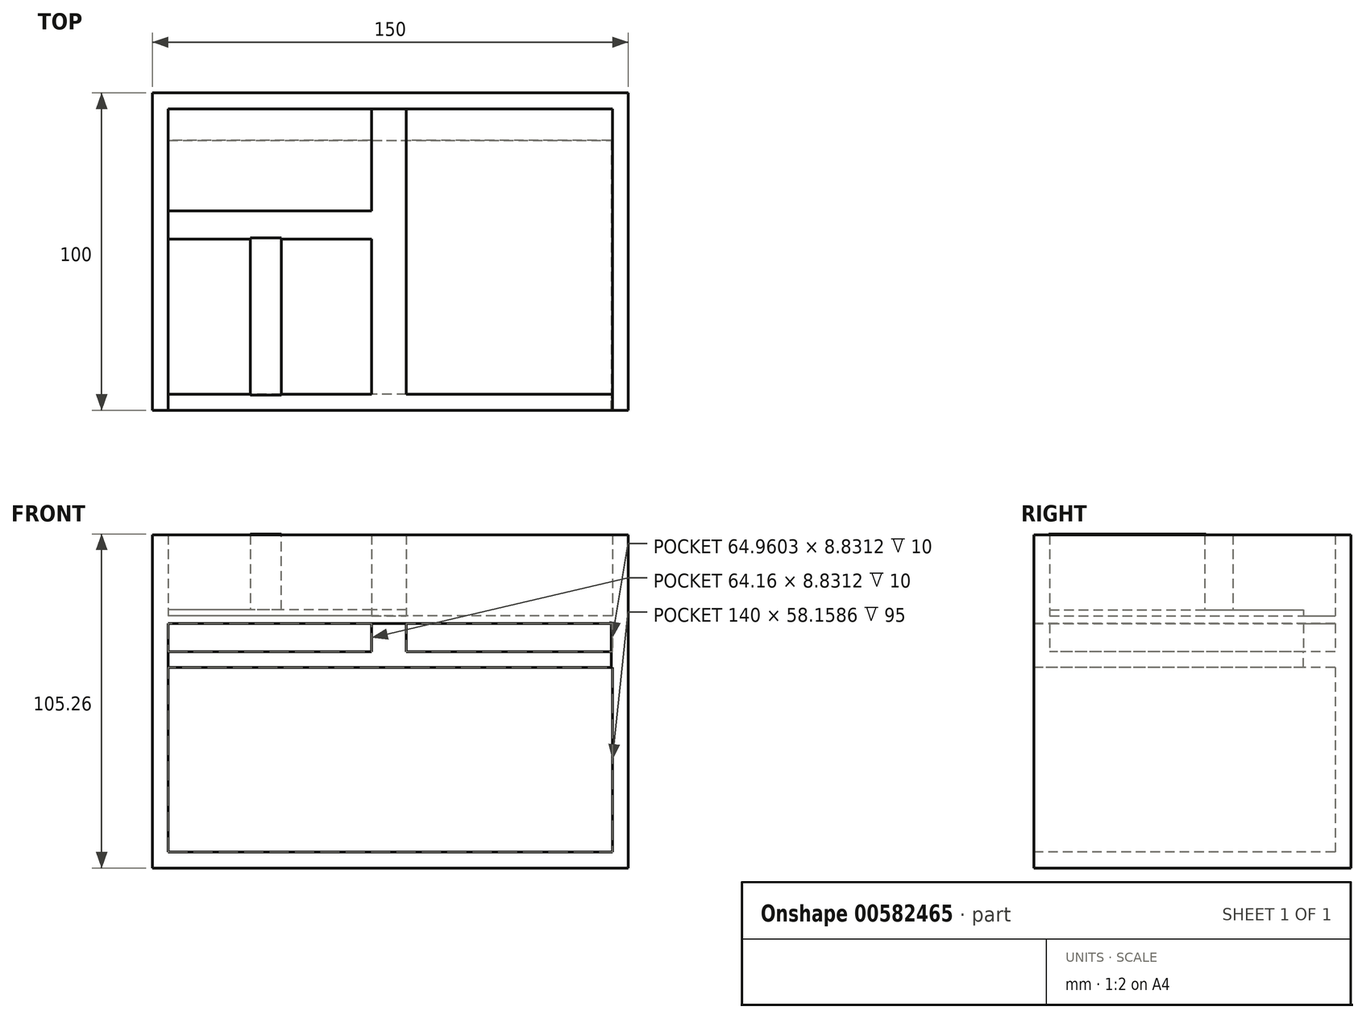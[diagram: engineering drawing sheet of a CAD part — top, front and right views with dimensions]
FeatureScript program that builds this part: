
annotation { "Feature Type Name" : "Feature", "Feature Type Description" : "" }
export const myFeature = defineFeature(function(context is Context, id is Id, definition is map)
    precondition{}
    {
        {
            var Q0;
            Q0=qCreatedBy(makeId("Top.planeOp"),FACE);
            var sketch = newSketch(context, id + "F0", { "sketchPlane" : qUnion([Q0])});
            skLineSegment(sketch, "E0.bottom", {"start": v(-111.6, 82.15) * mm, "end": v(38.4, 82.15) * mm});
            skLineSegment(sketch, "E0.top", {"start": v(-111.6, -17.85) * mm, "end": v(38.4, -17.85) * mm});
            skLineSegment(sketch, "E0.left", {"start": v(-111.6, 82.15) * mm, "end": v(-111.6, -17.85) * mm});
            skLineSegment(sketch, "E0.right", {"start": v(38.4, 82.15) * mm, "end": v(38.4, -17.85) * mm});
            skSolve(sketch);
        }
        {
            var Q0;
            Q0=makeQuery(id+"F0.imprint","IMPRINT",FACE,{"disambiguationData":[TD([[makeQuery(id+"F0.imprint","IMPRINT",EDGE,{"derivedFrom":sQuery(id+"F0.wireOp",EDGE,"E0.bottom")}),-1.0]])]});
            extrude(context, id + "F1", {"entities" : qUnion([Q0]), "depth" : 5 * mm, "offsetDistance" : 25 * mm});
        }
        {
            var Q0;
            Q0=makeQuery(id+"F1.opExtrude","CAP_FACE",FACE,{"disambiguationData":[OSD([sQuery(id+"F0.wireOp",EDGE,"E0.bottom"),sQuery(id+"F0.wireOp",EDGE,"E0.top"),sQuery(id+"F0.wireOp",EDGE,"E0.left"),sQuery(id+"F0.wireOp",EDGE,"E0.right")])],"isStart":false});
            var sketch = newSketch(context, id + "F2", { "sketchPlane" : qUnion([Q0])});
            skLineSegment(sketch, "E1.bottom", {"start": v(-111.6, 82.15) * mm, "end": v(-106.6, 82.15) * mm});
            skLineSegment(sketch, "E1.top", {"start": v(-111.6, -17.85) * mm, "end": v(-106.6, -17.85) * mm});
            skLineSegment(sketch, "E1.left", {"start": v(-111.6, 82.15) * mm, "end": v(-111.6, -17.85) * mm});
            skLineSegment(sketch, "E1.right", {"start": v(-106.6, 82.15) * mm, "end": v(-106.6, -17.85) * mm});
            skSolve(sketch);
        }
        {
            var Q0;
            Q0=makeQuery(id+"F2.imprint","IMPRINT",FACE,{"disambiguationData":[TD([[makeQuery(id+"F2.imprint","IMPRINT",EDGE,{"derivedFrom":sQuery(id+"F2.wireOp",EDGE,"E1.bottom")}),-1.0]])]});
            extrude(context, id + "F3", {"entities" : qUnion([Q0]), "operationType" : NewBodyOperationType.ADD, "depth" : 100 * mm, "offsetDistance" : 25 * mm});
        }
        {
            var Q0;
            Q0=makeQuery(id+"F1.opExtrude","CAP_FACE",FACE,{"disambiguationData":[OSD([sQuery(id+"F0.wireOp",EDGE,"E0.bottom"),sQuery(id+"F0.wireOp",EDGE,"E0.top"),sQuery(id+"F0.wireOp",EDGE,"E0.left"),sQuery(id+"F0.wireOp",EDGE,"E0.right")])],"isStart":false});
            var sketch = newSketch(context, id + "F4", { "sketchPlane" : qUnion([Q0])});
            skLineSegment(sketch, "E2.bottom", {"start": v(-106.6, 82.15) * mm, "end": v(38.4, 82.15) * mm});
            skLineSegment(sketch, "E2.top", {"start": v(-106.6, 77.15) * mm, "end": v(38.4, 77.15) * mm});
            skLineSegment(sketch, "E2.left", {"start": v(-106.6, 82.15) * mm, "end": v(-106.6, 77.15) * mm});
            skLineSegment(sketch, "E2.right", {"start": v(38.4, 82.15) * mm, "end": v(38.4, 77.15) * mm});
            skSolve(sketch);
        }
        {
            var Q0;
            Q0=makeQuery(id+"F4.imprint","IMPRINT",FACE,{"disambiguationData":[TD([[makeQuery(id+"F4.imprint","IMPRINT",EDGE,{"derivedFrom":sQuery(id+"F4.wireOp",EDGE,"E2.bottom")}),-1.0]])]});
            extrude(context, id + "F5", {"entities" : qUnion([Q0]), "operationType" : NewBodyOperationType.ADD, "depth" : 100 * mm, "offsetDistance" : 25 * mm});
        }
        {
            var Q0;
            Q0=makeQuery(id+"F1.opExtrude","CAP_FACE",FACE,{"disambiguationData":[OSD([sQuery(id+"F0.wireOp",EDGE,"E0.bottom"),sQuery(id+"F0.wireOp",EDGE,"E0.top"),sQuery(id+"F0.wireOp",EDGE,"E0.left"),sQuery(id+"F0.wireOp",EDGE,"E0.right")])],"isStart":false});
            var sketch = newSketch(context, id + "F6", { "sketchPlane" : qUnion([Q0])});
            skLineSegment(sketch, "E3.bottom", {"start": v(38.4, 77.15) * mm, "end": v(33.4, 77.15) * mm});
            skLineSegment(sketch, "E3.top", {"start": v(38.4, -17.85) * mm, "end": v(33.4, -17.85) * mm});
            skLineSegment(sketch, "E3.left", {"start": v(38.4, 77.15) * mm, "end": v(38.4, -17.85) * mm});
            skLineSegment(sketch, "E3.right", {"start": v(33.4, 77.15) * mm, "end": v(33.4, -17.85) * mm});
            skSolve(sketch);
        }
        {
            var Q0;
            Q0=makeQuery(id+"F6.imprint","IMPRINT",FACE,{"disambiguationData":[TD([[makeQuery(id+"F6.imprint","IMPRINT",EDGE,{"derivedFrom":sQuery(id+"F6.wireOp",EDGE,"E3.bottom")}),-1.0]])]});
            extrude(context, id + "F7", {"entities" : qUnion([Q0]), "operationType" : NewBodyOperationType.ADD, "depth" : 100 * mm, "offsetDistance" : 25 * mm});
        }
        {
            var Q0;
            Q0=makeQuery(id+"F7.boolean.opBoolean","MERGE",FACE,{"derivedFrom":[makeQuery(id+"F3.boolean.opBoolean","MERGE",FACE,{"derivedFrom":[makeQuery(id+"F1.opExtrude","SWEPT_FACE",FACE,{"disambiguationData":[OSD([sQuery(id+"F0.wireOp",EDGE,"E0.top")])]}),makeQuery(id+"F3.opExtrude","SWEPT_FACE",FACE,{"disambiguationData":[OSD([sQuery(id+"F2.wireOp",EDGE,"E1.top")])]})]}),makeQuery(id+"F7.opExtrude","SWEPT_FACE",FACE,{"disambiguationData":[OSD([sQuery(id+"F6.wireOp",EDGE,"E3.top")])]})]});
            var sketch = newSketch(context, id + "F8", { "sketchPlane" : qUnion([Q0])});
            skLineSegment(sketch, "E4.bottom", {"start": v(-106.6, 68.16) * mm, "end": v(33.4, 68.16) * mm});
            skLineSegment(sketch, "E4.top", {"start": v(-106.6, 63.16) * mm, "end": v(33.4, 63.16) * mm});
            skLineSegment(sketch, "E4.left", {"start": v(-106.6, 68.16) * mm, "end": v(-106.6, 63.16) * mm});
            skLineSegment(sketch, "E4.right", {"start": v(33.4, 68.16) * mm, "end": v(33.4, 63.16) * mm});
            skSolve(sketch);
        }
        {
            var Q0;
            Q0=makeQuery(id+"F8.imprint","IMPRINT",FACE,{"disambiguationData":[TD([[makeQuery(id+"F8.imprint","IMPRINT",EDGE,{"derivedFrom":sQuery(id+"F8.wireOp",EDGE,"E4.bottom")}),-1.0]])]});
            extrude(context, id + "F9", {"entities" : qUnion([Q0]), "operationType" : NewBodyOperationType.ADD, "oppositeDirection" : true, "depth" : 100 * mm, "offsetDistance" : 25 * mm});
        }
        {
            var Q0;
            Q0=makeQuery(id+"F9.opExtrude","SWEPT_FACE",FACE,{"disambiguationData":[OSD([sQuery(id+"F8.wireOp",EDGE,"E4.bottom")])]});
            var sketch = newSketch(context, id + "F10", { "sketchPlane" : qUnion([Q0])});
            skLineSegment(sketch, "E5.bottom", {"start": v(-106.6, -17.85) * mm, "end": v(33.4, -17.85) * mm});
            skLineSegment(sketch, "E5.top", {"start": v(-106.6, -12.85) * mm, "end": v(33.4, -12.85) * mm});
            skLineSegment(sketch, "E5.left", {"start": v(-106.6, -17.85) * mm, "end": v(-106.6, -12.85) * mm});
            skLineSegment(sketch, "E5.right", {"start": v(33.4, -17.85) * mm, "end": v(33.4, -12.85) * mm});
            skSolve(sketch);
        }
        {
            var Q0;
            Q0=makeQuery(id+"F10.imprint","IMPRINT",FACE,{"disambiguationData":[TD([[makeQuery(id+"F10.imprint","IMPRINT",EDGE,{"derivedFrom":sQuery(id+"F10.wireOp",EDGE,"E5.bottom")}),1.0]])]});
            extrude(context, id + "F11", {"entities" : qUnion([Q0]), "operationType" : NewBodyOperationType.ADD, "depth" : 36.8 * mm, "offsetDistance" : 25 * mm});
        }
        {
            var Q0;
            Q0=makeQuery(id+"F9.opExtrude","SWEPT_FACE",FACE,{"disambiguationData":[OSD([sQuery(id+"F8.wireOp",EDGE,"E4.bottom")])]});
            var sketch = newSketch(context, id + "F12", { "sketchPlane" : qUnion([Q0])});
            skLineSegment(sketch, "E6.bottom", {"start": v(-42.44, 77.15) * mm, "end": v(-31.56, 77.15) * mm});
            skLineSegment(sketch, "E6.top", {"start": v(-42.44, -12.85) * mm, "end": v(-31.56, -12.85) * mm});
            skLineSegment(sketch, "E6.left", {"start": v(-42.44, 77.15) * mm, "end": v(-42.44, -12.85) * mm});
            skLineSegment(sketch, "E6.right", {"start": v(-31.56, 77.15) * mm, "end": v(-31.56, -12.85) * mm});
            skSolve(sketch);
        }
        {
            var Q0;
            Q0=makeQuery(id+"F12.imprint","IMPRINT",FACE,{"disambiguationData":[TD([[makeQuery(id+"F12.imprint","IMPRINT",EDGE,{"derivedFrom":sQuery(id+"F12.wireOp",EDGE,"E6.bottom")}),1.0]])]});
            extrude(context, id + "F13", {"entities" : qUnion([Q0]), "operationType" : NewBodyOperationType.ADD, "depth" : 36.8 * mm, "offsetDistance" : 25 * mm});
        }
        {
            var Q0;
            Q0=makeQuery(id+"F13.boolean.opBoolean","SPLIT",FACE,{"disambiguationData":[TD([makeQuery(id+"F3.opExtrude","SWEPT_FACE",FACE,{"disambiguationData":[OSD([sQuery(id+"F2.wireOp",EDGE,"E1.right")])]})])],"derivedFrom":makeQuery(id+"F9.opExtrude","SWEPT_FACE",FACE,{"disambiguationData":[OSD([sQuery(id+"F8.wireOp",EDGE,"E4.bottom")])]})});
            var sketch = newSketch(context, id + "F14", { "sketchPlane" : qUnion([Q0])});
            skSolve(sketch);
        }
        {
            var Q0;
            {var subQ2=sQuery(id+"F12.wireOp",EDGE,"E6.left");Q0=makeQuery(id+"F14.imprint","IMPRINT",FACE,{"disambiguationData":[TD([[makeQuery(id+"F14.imprint","IMPRINT",EDGE,{"derivedFrom":makeQuery(id+"F13.opExtrude","CAP_EDGE",EDGE,{"disambiguationData":[OSD([subQ2])],"isStart":true})}),-1.0]])]});}
            var sketch = newSketch(context, id + "F15", { "sketchPlane" : qUnion([Q0])});
            skLineSegment(sketch, "E7.bottom", {"start": v(-106.58, 44.94) * mm, "end": v(33.5, 44.94) * mm});
            skLineSegment(sketch, "E7.top", {"start": v(-106.58, 36.1) * mm, "end": v(33.5, 36.1) * mm});
            skLineSegment(sketch, "E7.left", {"start": v(-106.58, 44.94) * mm, "end": v(-106.58, 36.1) * mm});
            skLineSegment(sketch, "E7.right", {"start": v(33.5, 44.94) * mm, "end": v(33.5, 36.1) * mm});
            skSolve(sketch);
        }
        {
            var Q0;
            {var subQ0=sQuery(id+"F15.wireOp",EDGE,"E7.left");Q0=makeQuery(id+"F15.imprint","IMPRINT",FACE,{"disambiguationData":[TD([[makeQuery(id+"F15.imprint","IMPRINT",EDGE,{"derivedFrom":subQ0}),1.0]])]});}
            extrude(context, id + "F16", {"entities" : qUnion([Q0]), "operationType" : NewBodyOperationType.ADD, "depth" : 36.8 * mm, "offsetDistance" : 25 * mm});
        }
        {
            var Q0;
            {var subQ2=sQuery(id+"F12.wireOp",EDGE,"E6.left");Q0=makeQuery(id+"F14.imprint","IMPRINT",FACE,{"disambiguationData":[TD([[makeQuery(id+"F14.imprint","IMPRINT",EDGE,{"derivedFrom":makeQuery(id+"F13.opExtrude","CAP_EDGE",EDGE,{"disambiguationData":[OSD([subQ2])],"isStart":true})}),-1.0]])]});}
            var sketch = newSketch(context, id + "F17", { "sketchPlane" : qUnion([Q0])});
            skLineSegment(sketch, "E8.bottom", {"start": v(-80.74, 35.42) * mm, "end": v(-71, 35.42) * mm});
            skLineSegment(sketch, "E8.top", {"start": v(-80.74, -13.08) * mm, "end": v(-71, -13.08) * mm});
            skLineSegment(sketch, "E8.left", {"start": v(-80.74, 35.42) * mm, "end": v(-80.74, -13.08) * mm});
            skLineSegment(sketch, "E8.right", {"start": v(-71, 35.42) * mm, "end": v(-71, -13.08) * mm});
            skSolve(sketch);
        }
        {
            var Q0;
            Q0 = qSketchRegion(id + "F17", true);
            extrude(context, id + "F18", {"entities" : qUnion([Q0]), "operationType" : NewBodyOperationType.ADD, "depth" : 37.1 * mm, "offsetDistance" : 25 * mm});
        }
        {
            var Q0;
            Q0=makeQuery(id+"F18.opExtrude","SWEPT_FACE",FACE,{"disambiguationData":[OSD([sQuery(id+"F17.wireOp",EDGE,"E8.bottom")])]});
            extrude(context, id + "F19", {"entities" : qUnion([Q0]), "operationType" : NewBodyOperationType.ADD, "depth" : 1 * mm, "offsetDistance" : 25 * mm});
        }
        {
            var Q0;
            Q0=makeQuery(id+"F11.boolean.opBoolean","MERGE",FACE,{"derivedFrom":[makeQuery(id+"F9.boolean.opBoolean","MERGE",FACE,{"derivedFrom":[makeQuery(id+"F7.boolean.opBoolean","MERGE",FACE,{"derivedFrom":[makeQuery(id+"F3.boolean.opBoolean","MERGE",FACE,{"derivedFrom":[makeQuery(id+"F1.opExtrude","SWEPT_FACE",FACE,{"disambiguationData":[OSD([sQuery(id+"F0.wireOp",EDGE,"E0.top")])]}),makeQuery(id+"F3.opExtrude","SWEPT_FACE",FACE,{"disambiguationData":[OSD([sQuery(id+"F2.wireOp",EDGE,"E1.top")])]})]}),makeQuery(id+"F7.opExtrude","SWEPT_FACE",FACE,{"disambiguationData":[OSD([sQuery(id+"F6.wireOp",EDGE,"E3.top")])]})]}),makeQuery(id+"F9.opExtrude","CAP_FACE",FACE,{"disambiguationData":[OSD([sQuery(id+"F8.wireOp",EDGE,"E4.bottom"),sQuery(id+"F8.wireOp",EDGE,"E4.top"),sQuery(id+"F8.wireOp",EDGE,"E4.left"),sQuery(id+"F8.wireOp",EDGE,"E4.right")])],"isStart":true})]}),makeQuery(id+"F11.opExtrude","SWEPT_FACE",FACE,{"disambiguationData":[OSD([sQuery(id+"F10.wireOp",EDGE,"E5.bottom")])]})]});
            var sketch = newSketch(context, id + "F20", { "sketchPlane" : qUnion([Q0])});
            skLineSegment(sketch, "E9.bottom", {"start": v(-106.6, 63.16) * mm, "end": v(33.03, 63.16) * mm});
            skLineSegment(sketch, "E9.top", {"start": v(-106.6, 81.4) * mm, "end": v(33.03, 81.4) * mm});
            skLineSegment(sketch, "E9.left", {"start": v(-106.6, 63.16) * mm, "end": v(-106.6, 81.4) * mm});
            skLineSegment(sketch, "E9.right", {"start": v(33.03, 63.16) * mm, "end": v(33.03, 81.4) * mm});
            skSolve(sketch);
        }
        {
            var Q0;
            Q0=makeQuery(id+"F20.imprint","IMPRINT",FACE,{"disambiguationData":[TD([[makeQuery(id+"F20.imprint","IMPRINT",EDGE,{"derivedFrom":sQuery(id+"F20.wireOp",EDGE,"E9.bottom")}),1.0]])]});
            extrude(context, id + "F21", {"entities" : qUnion([Q0]), "operationType" : NewBodyOperationType.REMOVE, "oppositeDirection" : true, "depth" : 85 * mm, "offsetDistance" : 25 * mm});
        }
        {
            var Q0;
            {var subQ3=sQuery(id+"F2.wireOp",EDGE,"E1.right");var subQ9=sQuery(id+"F8.wireOp",EDGE,"E4.bottom");var subQ10=sQuery(id+"F8.wireOp",EDGE,"E4.top");var subQ12=makeQuery(id+"F3.opExtrude","SWEPT_FACE",FACE,{"disambiguationData":[OSD([subQ3])]});Q0=makeQuery(id+"F21.boolean.opBoolean","MERGE",FACE,{"derivedFrom":[makeQuery(id+"F9.boolean.opBoolean","SPLIT",FACE,{"disambiguationData":[TD([makeQuery(id+"F9.opExtrude","SWEPT_FACE",FACE,{"disambiguationData":[OSD([subQ10])]})])],"derivedFrom":subQ12}),makeQuery(id+"F9.boolean.opBoolean","SPLIT",FACE,{"disambiguationData":[TD([makeQuery(id+"F9.opExtrude","SWEPT_FACE",FACE,{"disambiguationData":[OSD([subQ9])]})])],"derivedFrom":subQ12}),makeQuery(id+"F21.opExtrude","SWEPT_FACE",FACE,{"disambiguationData":[OSD([sQuery(id+"F20.wireOp",EDGE,"E9.left")])]})]});}
            var sketch = newSketch(context, id + "F22", { "sketchPlane" : qUnion([Q0])});
            skLineSegment(sketch, "E10.bottom", {"start": v(77.15, 79.5) * mm, "end": v(-17.85, 79.5) * mm});
            skLineSegment(sketch, "E10.top", {"start": v(77.15, 76.99) * mm, "end": v(-17.85, 76.99) * mm});
            skLineSegment(sketch, "E10.left", {"start": v(77.15, 79.5) * mm, "end": v(77.15, 76.99) * mm});
            skLineSegment(sketch, "E10.right", {"start": v(-17.85, 79.5) * mm, "end": v(-17.85, 76.99) * mm});
            skSolve(sketch);
        }
        {
            var Q0;
            Q0=makeQuery(id+"F22.imprint","IMPRINT",FACE,{"disambiguationData":[TD([[makeQuery(id+"F22.imprint","IMPRINT",EDGE,{"derivedFrom":sQuery(id+"F22.wireOp",EDGE,"E10.bottom")}),1.0]])]});
            extrude(context, id + "F23", {"entities" : qUnion([Q0]), "operationType" : NewBodyOperationType.ADD, "depth" : 142.2 * mm, "offsetDistance" : 25 * mm});
        }
        {
            var Q0;
            Q0=makeQuery(id+"F21.boolean.opBoolean","COPY",FACE,{"derivedFrom":makeQuery(id+"F21.opExtrude","SWEPT_FACE",FACE,{"disambiguationData":[OSD([sQuery(id+"F20.wireOp",EDGE,"E9.top")])]})});
            var sketch = newSketch(context, id + "F24", { "sketchPlane" : qUnion([Q0])});
            skLineSegment(sketch, "E11.bottom", {"start": v(-106.6, 17.85) * mm, "end": v(33.03, 17.85) * mm});
            skLineSegment(sketch, "E11.top", {"start": v(-106.6, 12.85) * mm, "end": v(33.03, 12.85) * mm});
            skLineSegment(sketch, "E11.left", {"start": v(-106.6, 17.85) * mm, "end": v(-106.6, 12.85) * mm});
            skLineSegment(sketch, "E11.right", {"start": v(33.03, 17.85) * mm, "end": v(33.03, 12.85) * mm});
            skSolve(sketch);
        }
        {
            var Q0;
            Q0=makeQuery(id+"F24.imprint","IMPRINT",FACE,{"disambiguationData":[TD([[makeQuery(id+"F24.imprint","IMPRINT",EDGE,{"derivedFrom":sQuery(id+"F24.wireOp",EDGE,"E11.bottom")}),-1.0]])]});
            extrude(context, id + "F25", {"entities" : qUnion([Q0]), "operationType" : NewBodyOperationType.ADD, "depth" : 3 * mm, "offsetDistance" : 25 * mm});
        }
    });
